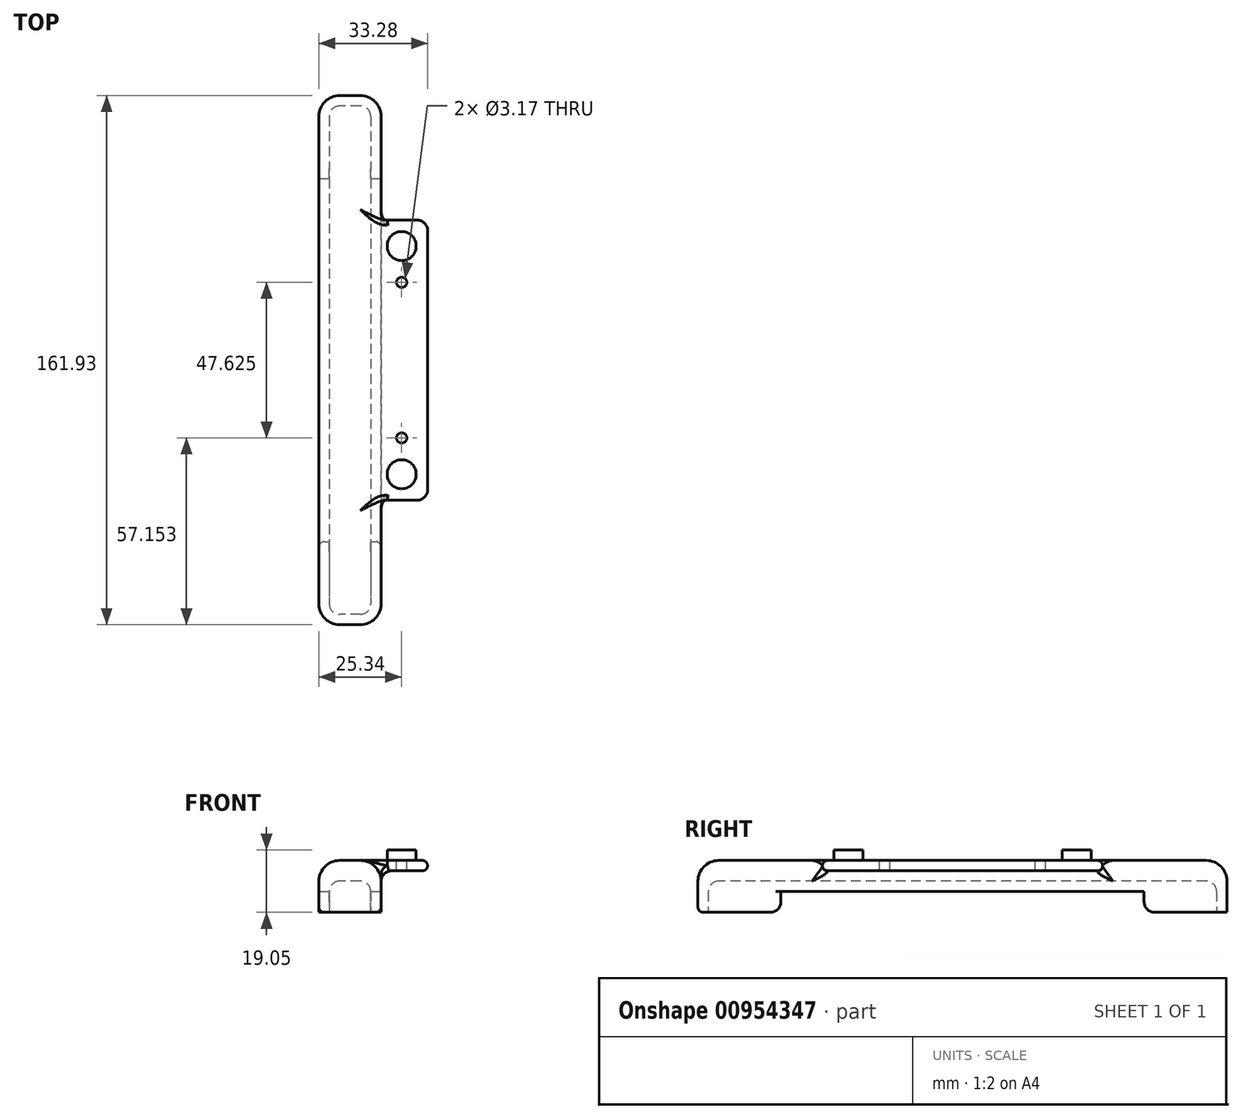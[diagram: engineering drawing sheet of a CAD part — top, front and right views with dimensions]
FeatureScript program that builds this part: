
annotation { "Feature Type Name" : "Feature", "Feature Type Description" : "" }
export const myFeature = defineFeature(function(context is Context, id is Id, definition is map)
    precondition{}
    {
        {
            var Q0;
            Q0=qCreatedBy(makeId("Top.planeOp"),FACE);
            var sketch = newSketch(context, id + "F0", { "sketchPlane" : qUnion([Q0])});
            skLineSegment(sketch, "E0.bottom", {"start": v(7.94, 7.94) * mm, "end": v(-25.34, 7.94) * mm});
            skLineSegment(sketch, "E0.top", {"start": v(7.94, -77.79) * mm, "end": v(-25.34, -77.79) * mm});
            skLineSegment(sketch, "E0.left", {"start": v(7.94, 7.94) * mm, "end": v(7.94, -77.79) * mm});
            skLineSegment(sketch, "E0.right", {"start": v(-25.34, 7.94) * mm, "end": v(-25.34, -77.79) * mm});
            skCircle(sketch, "E1", {"center": v(0, 0) * mm, "radius": 4.45 * mm});
            skCircle(sketch, "E2", {"center": v(0, -69.85) * mm, "radius": 4.45 * mm});
            skSolve(sketch);
        }
        {
            var Q0;
            Q0=makeQuery(id+"F0.imprint","IMPRINT",FACE,{"disambiguationData":[TD([[makeQuery(id+"F0.imprint","IMPRINT",EDGE,{"derivedFrom":sQuery(id+"F0.wireOp",EDGE,"E0.bottom")}),1.0]])]});
            extrude(context, id + "F1", {"entities" : qUnion([Q0]), "depth" : 3.17 * mm, "offsetDistance" : 25.4 * mm});
        }
        {
            var Q0;
            Q0=makeQuery(id+"F1.opExtrude","CAP_FACE",FACE,{"disambiguationData":[OSD([sQuery(id+"F0.wireOp",EDGE,"E0.bottom"),sQuery(id+"F0.wireOp",EDGE,"E0.top"),sQuery(id+"F0.wireOp",EDGE,"E0.left"),sQuery(id+"F0.wireOp",EDGE,"E0.right"),sQuery(id+"F0.wireOp",EDGE,"E1"),sQuery(id+"F0.wireOp",EDGE,"E2"),sQuery(id+"F0.wireOp",EDGE,"2b3a6ad9-cd32-4de6-a3de-1586ba308fc8.0"),sQuery(id+"F0.wireOp",EDGE,"b44657c2-62e0-4c01-9275-96e163e3740f.0"),sQuery(id+"F0.wireOp",EDGE,"936a78f3-9829-4f7b-97c9-a64f973ed5e6.0"),sQuery(id+"F0.wireOp",EDGE,"a6370155-7cf4-457e-acdf-fc1a374a136d.trimOffspring")])],"isStart":true});
            var sketch = newSketch(context, id + "F2", { "sketchPlane" : qUnion([Q0])});
            skCircle(sketch, "E3.0", {"center": v(0, 0) * mm, "radius": 4.45 * mm});
            skCircle(sketch, "E3.1", {"center": v(0, 69.85) * mm, "radius": 4.45 * mm});
            skSolve(sketch);
        }
        {
            var Q0;
            Q0 = qSketchRegion(id + "F2", true);
            extrude(context, id + "F3", {"entities" : qUnion([Q0]), "operationType" : NewBodyOperationType.ADD, "oppositeDirection" : true, "depth" : 6.35 * mm, "offsetDistance" : 25.4 * mm});
        }
        {
            var Q0;
            Q0=makeQuery(id+"F3.boolean.opBoolean","MERGE",FACE,{"derivedFrom":[makeQuery(id+"F1.opExtrude","CAP_FACE",FACE,{"disambiguationData":[OSD([sQuery(id+"F0.wireOp",EDGE,"E0.bottom"),sQuery(id+"F0.wireOp",EDGE,"E0.top"),sQuery(id+"F0.wireOp",EDGE,"E0.left"),sQuery(id+"F0.wireOp",EDGE,"E0.right"),sQuery(id+"F0.wireOp",EDGE,"E1"),sQuery(id+"F0.wireOp",EDGE,"E2")])],"isStart":true}),makeQuery(id+"F3.opExtrude","CAP_FACE",FACE,{"disambiguationData":[OSD([sQuery(id+"F2.wireOp",EDGE,"E3.0")])],"isStart":true}),makeQuery(id+"F3.opExtrude","CAP_FACE",FACE,{"disambiguationData":[OSD([sQuery(id+"F2.wireOp",EDGE,"E3.1")])],"isStart":true})]});
            var sketch = newSketch(context, id + "F4", { "sketchPlane" : qUnion([Q0])});
            skLineSegment(sketch, "E4.bottom", {"start": v(-25.34, -46.04) * mm, "end": v(-6.29, -46.04) * mm});
            skLineSegment(sketch, "E4.top", {"start": v(-25.34, 115.89) * mm, "end": v(-6.29, 115.89) * mm});
            skLineSegment(sketch, "E4.left", {"start": v(-25.34, -46.04) * mm, "end": v(-25.34, 115.89) * mm});
            skLineSegment(sketch, "E4.right", {"start": v(-6.29, -46.04) * mm, "end": v(-6.29, 115.89) * mm});
            skSolve(sketch);
        }
        {
            var Q0;
            Q0 = qSketchRegion(id + "F4", true);
            var Q1;
            Q1=makeQuery(id+"F1.opExtrude","CAP_FACE",FACE,{"disambiguationData":[OSD([sQuery(id+"F0.wireOp",EDGE,"E0.bottom"),sQuery(id+"F0.wireOp",EDGE,"E0.top"),sQuery(id+"F0.wireOp",EDGE,"E0.left"),sQuery(id+"F0.wireOp",EDGE,"E0.right"),sQuery(id+"F0.wireOp",EDGE,"E1"),sQuery(id+"F0.wireOp",EDGE,"E2")])],"isStart":false});
            extrude(context, id + "F5", {"entities" : qUnion([Q0]), "operationType" : NewBodyOperationType.ADD, "depth" : 6.35 * mm, "offsetDistance" : 25.4 * mm, "hasSecondDirection" : true, "secondDirectionBound" : SecondDirectionBoundingType.UP_TO_SURFACE, "secondDirectionOppositeDirection" : true, "secondDirectionDepth" : 25.4 * mm, "secondDirectionBoundEntityFace" : qUnion([Q1])});
        }
        {
            var Q0;
            Q0=makeQuery(id+"F5.opExtrude","CAP_FACE",FACE,{"disambiguationData":[OSD([sQuery(id+"F4.wireOp",EDGE,"E4.bottom"),sQuery(id+"F4.wireOp",EDGE,"E4.top"),sQuery(id+"F4.wireOp",EDGE,"E4.left"),sQuery(id+"F4.wireOp",EDGE,"E4.right")])],"isStart":false});
            var sketch = newSketch(context, id + "F6", { "sketchPlane" : qUnion([Q0])});
            skLineSegment(sketch, "E5.bottom", {"start": v(-25.34, -46.04) * mm, "end": v(-6.29, -46.04) * mm});
            skLineSegment(sketch, "E5.top", {"start": v(-25.34, -20.64) * mm, "end": v(-6.29, -20.64) * mm});
            skLineSegment(sketch, "E5.left", {"start": v(-25.34, -46.04) * mm, "end": v(-25.34, -20.64) * mm});
            skLineSegment(sketch, "E5.right", {"start": v(-6.29, -46.04) * mm, "end": v(-6.29, -20.64) * mm});
            skLineSegment(sketch, "E6.bottom", {"start": v(-25.34, 115.89) * mm, "end": v(-6.29, 115.89) * mm});
            skLineSegment(sketch, "E6.top", {"start": v(-25.34, 90.49) * mm, "end": v(-6.29, 90.49) * mm});
            skLineSegment(sketch, "E6.left", {"start": v(-25.34, 115.89) * mm, "end": v(-25.34, 90.49) * mm});
            skLineSegment(sketch, "E6.right", {"start": v(-6.29, 115.89) * mm, "end": v(-6.29, 90.49) * mm});
            skSolve(sketch);
        }
        {
            var Q0;
            Q0 = qSketchRegion(id + "F6", true);
            extrude(context, id + "F7", {"entities" : qUnion([Q0]), "operationType" : NewBodyOperationType.ADD, "depth" : 6.35 * mm, "offsetDistance" : 25.4 * mm});
        }
        {
            var Q0;
            Q0=makeQuery(id+"F5.boolean.opBoolean","MERGE",EDGE,{"derivedFrom":[makeQuery(id+"F1.opExtrude","CAP_EDGE",EDGE,{"disambiguationData":[OSD([sQuery(id+"F0.wireOp",EDGE,"E0.right")])],"isStart":false}),makeQuery(id+"F5.opExtrude","CAP_EDGE",EDGE,{"disambiguationData":[OSD([sQuery(id+"F4.wireOp",EDGE,"E4.left")])],"isStart":true})]});
            var Q1;
            {var subQ1=sQuery(id+"F4.wireOp",EDGE,"E4.right");var subQ2=sQuery(id+"F0.wireOp",EDGE,"E0.bottom");Q1=makeQuery(id+"F5.boolean.opBoolean","SPLIT",EDGE,{"disambiguationData":[TD([makeQuery(id+"F1.opExtrude","SWEPT_FACE",FACE,{"disambiguationData":[OSD([subQ2])]})])],"derivedFrom":makeQuery(id+"F5.opExtrude","CAP_EDGE",EDGE,{"disambiguationData":[OSD([subQ1])],"isStart":true})});}
            var Q2;
            Q2=makeQuery(id+"F5.opExtrude","CAP_EDGE",EDGE,{"disambiguationData":[OSD([sQuery(id+"F4.wireOp",EDGE,"E4.bottom")])],"isStart":true});
            var Q3;
            Q3=makeQuery(id+"F7.boolean.opBoolean","MERGE",EDGE,{"derivedFrom":[makeQuery(id+"F5.opExtrude","SWEPT_EDGE",EDGE,{"disambiguationData":[OSD([sQuery(id+"F4.wireOp",EDGE,"E4.bottom"),sQuery(id+"F4.wireOp",EDGE,"E4.right")])]}),makeQuery(id+"F7.opExtrude","SWEPT_EDGE",EDGE,{"disambiguationData":[OSD([sQuery(id+"F6.wireOp",EDGE,"E5.bottom"),sQuery(id+"F6.wireOp",EDGE,"E5.right")])]})]});
            var Q4;
            Q4=makeQuery(id+"F7.boolean.opBoolean","MERGE",EDGE,{"derivedFrom":[makeQuery(id+"F5.opExtrude","SWEPT_EDGE",EDGE,{"disambiguationData":[OSD([sQuery(id+"F4.wireOp",EDGE,"E4.bottom"),sQuery(id+"F4.wireOp",EDGE,"E4.left")])]}),makeQuery(id+"F7.opExtrude","SWEPT_EDGE",EDGE,{"disambiguationData":[OSD([sQuery(id+"F6.wireOp",EDGE,"E5.bottom"),sQuery(id+"F6.wireOp",EDGE,"E5.left")])]})]});
            var Q5;
            Q5=makeQuery(id+"F7.boolean.opBoolean","MERGE",EDGE,{"derivedFrom":[makeQuery(id+"F5.opExtrude","SWEPT_EDGE",EDGE,{"disambiguationData":[OSD([sQuery(id+"F4.wireOp",EDGE,"E4.top"),sQuery(id+"F4.wireOp",EDGE,"E4.left")])]}),makeQuery(id+"F7.opExtrude","SWEPT_EDGE",EDGE,{"disambiguationData":[OSD([sQuery(id+"F6.wireOp",EDGE,"E6.bottom"),sQuery(id+"F6.wireOp",EDGE,"E6.left")])]})]});
            fillet(context, id + "F8", {"entities" : qUnion([Q0, Q1, Q2, Q3, Q4, Q5]), "radius" : 6.35 * mm, "allowEdgeOverflow" : false});
        }
        {
            var Q0;
            Q0=makeQuery(id+"F5.opExtrude","CAP_EDGE",EDGE,{"disambiguationData":[OSD([sQuery(id+"F4.wireOp",EDGE,"E4.top")])],"isStart":true});
            fillet(context, id + "F9", {"entities" : qUnion([Q0]), "radius" : 6.35 * mm, "tangentPropagation" : true, "allowEdgeOverflow" : false});
        }
        {
            var Q0;
            Q0=makeQuery(id+"F7.opExtrude","CAP_FACE",FACE,{"disambiguationData":[OSD([sQuery(id+"F6.wireOp",EDGE,"E5.bottom"),sQuery(id+"F6.wireOp",EDGE,"E5.top"),sQuery(id+"F6.wireOp",EDGE,"E5.left"),sQuery(id+"F6.wireOp",EDGE,"E5.right")])],"isStart":false});
            var sketch = newSketch(context, id + "F10", { "sketchPlane" : qUnion([Q0])});
            skLineSegment(sketch, "E7.bottom", {"start": v(-12.64, -42.86) * mm, "end": v(-18.99, -42.86) * mm});
            skLineSegment(sketch, "E7.top", {"start": v(-12.64, 112.71) * mm, "end": v(-18.99, 112.71) * mm});
            skLineSegment(sketch, "E7.left", {"start": v(-9.46, -39.69) * mm, "end": v(-9.46, 109.54) * mm});
            skLineSegment(sketch, "E7.right", {"start": v(-22.16, -39.69) * mm, "end": v(-22.16, 109.54) * mm});
            skPoint(sketch, "E8.visualSharp", {"position": v(-9.46, -42.86) * mm});
            skArc(sketch, "E8.filletArc", {"start": v(-12.64, -42.86) * mm, "mid": v(-10.4, -41.93) * mm, "end": v(-9.46, -39.69) * mm});
            skPoint(sketch, "E9.visualSharp", {"position": v(-22.16, -42.86) * mm});
            skArc(sketch, "E9.filletArc", {"start": v(-22.16, -39.69) * mm, "mid": v(-21.23, -41.93) * mm, "end": v(-18.99, -42.86) * mm});
            skPoint(sketch, "E10.visualSharp", {"position": v(-9.46, 112.71) * mm});
            skArc(sketch, "E10.filletArc", {"start": v(-9.46, 109.54) * mm, "mid": v(-10.4, 111.78) * mm, "end": v(-12.64, 112.71) * mm});
            skPoint(sketch, "E11.visualSharp", {"position": v(-22.16, 112.71) * mm});
            skArc(sketch, "E11.filletArc", {"start": v(-18.99, 112.71) * mm, "mid": v(-21.23, 111.78) * mm, "end": v(-22.16, 109.54) * mm});
            skSolve(sketch);
        }
        {
            var Q0;
            Q0 = qSketchRegion(id + "F10", true);
            extrude(context, id + "F11", {"entities" : qUnion([Q0]), "operationType" : NewBodyOperationType.REMOVE, "oppositeDirection" : true, "depth" : 9.52 * mm, "offsetDistance" : 25.4 * mm});
        }
        {
            var Q0;
            {var subQ0=sQuery(id+"F0.wireOp",EDGE,"E0.top");var subQ2=sQuery(id+"F4.wireOp",EDGE,"E4.right");var subQ3=sQuery(id+"F0.wireOp",EDGE,"E0.bottom");Q0=makeQuery(id+"F8.opFillet","BLEND_EDGE",EDGE,{"blendedFrom":[makeQuery(id+"F5.boolean.opBoolean","SPLIT",EDGE,{"disambiguationData":[TD([makeQuery(id+"F1.opExtrude","SWEPT_FACE",FACE,{"disambiguationData":[OSD([subQ3])]})])],"derivedFrom":makeQuery(id+"F5.opExtrude","CAP_EDGE",EDGE,{"disambiguationData":[OSD([subQ2])],"isStart":true})}),makeQuery(id+"F1.opExtrude","SWEPT_FACE",FACE,{"disambiguationData":[OSD([subQ0])]})],"blendedInto":[makeQuery(id+"F1.opExtrude","SWEPT_FACE",FACE,{"disambiguationData":[OSD([subQ0])]})]});}
            var Q1;
            Q1=makeQuery(id+"F1.opExtrude","SWEPT_EDGE",EDGE,{"disambiguationData":[OSD([sQuery(id+"F0.wireOp",EDGE,"E0.top"),sQuery(id+"F0.wireOp",EDGE,"E0.left")])]});
            var Q2;
            Q2=makeQuery(id+"F1.opExtrude","SWEPT_EDGE",EDGE,{"disambiguationData":[OSD([sQuery(id+"F0.wireOp",EDGE,"E0.bottom"),sQuery(id+"F0.wireOp",EDGE,"E0.left")])]});
            var Q3;
            {var subQ0=sQuery(id+"F0.wireOp",EDGE,"E0.bottom");var subQ1=makeQuery(id+"F1.opExtrude","SWEPT_FACE",FACE,{"disambiguationData":[OSD([subQ0])]});var subQ3=sQuery(id+"F4.wireOp",EDGE,"E4.right");Q3=makeQuery(id+"F8.opFillet","BLEND_EDGE",EDGE,{"blendedFrom":[makeQuery(id+"F5.boolean.opBoolean","SPLIT",EDGE,{"disambiguationData":[TD([subQ1])],"derivedFrom":makeQuery(id+"F5.opExtrude","CAP_EDGE",EDGE,{"disambiguationData":[OSD([subQ3])],"isStart":true})}),subQ1],"blendedInto":[subQ1]});}
            var Q4;
            {var subQ0=sQuery(id+"F6.wireOp",EDGE,"E5.top");Q4=makeQuery(id+"F11.boolean.opBoolean","SPLIT",EDGE,{"disambiguationData":[TD([makeQuery(id+"F1.opExtrude","SWEPT_FACE",FACE,{"disambiguationData":[OSD([sQuery(id+"F0.wireOp",EDGE,"E0.right")])]})])],"derivedFrom":makeQuery(id+"F7.opExtrude","CAP_EDGE",EDGE,{"disambiguationData":[OSD([subQ0])],"isStart":false})});}
            var Q5;
            {var subQ0=sQuery(id+"F6.wireOp",EDGE,"E5.top");Q5=makeQuery(id+"F11.boolean.opBoolean","SPLIT",EDGE,{"disambiguationData":[TD([makeQuery(id+"F1.opExtrude","SWEPT_FACE",FACE,{"disambiguationData":[OSD([sQuery(id+"F0.wireOp",EDGE,"E0.right")])]})])],"derivedFrom":makeQuery(id+"F7.opExtrude","CAP_EDGE",EDGE,{"disambiguationData":[OSD([subQ0])],"isStart":true})});}
            var Q6;
            {var subQ1=sQuery(id+"F6.wireOp",EDGE,"E5.top");Q6=makeQuery(id+"F11.boolean.opBoolean","SPLIT",EDGE,{"disambiguationData":[TD([makeQuery(id+"F5.opExtrude","SWEPT_FACE",FACE,{"disambiguationData":[OSD([sQuery(id+"F4.wireOp",EDGE,"E4.right")])]})])],"derivedFrom":makeQuery(id+"F7.opExtrude","CAP_EDGE",EDGE,{"disambiguationData":[OSD([subQ1])],"isStart":false})});}
            var Q7;
            {var subQ0=sQuery(id+"F4.wireOp",EDGE,"E4.right");var subQ1=sQuery(id+"F6.wireOp",EDGE,"E5.top");Q7=makeQuery(id+"F11.boolean.opBoolean","SPLIT",EDGE,{"disambiguationData":[TD([makeQuery(id+"F5.opExtrude","SWEPT_FACE",FACE,{"disambiguationData":[OSD([subQ0])]})])],"derivedFrom":makeQuery(id+"F7.opExtrude","CAP_EDGE",EDGE,{"disambiguationData":[OSD([subQ1])],"isStart":true})});}
            var Q8;
            {var subQ0=sQuery(id+"F6.wireOp",EDGE,"E6.top");Q8=makeQuery(id+"F11.boolean.opBoolean","SPLIT",EDGE,{"disambiguationData":[TD([makeQuery(id+"F5.opExtrude","SWEPT_FACE",FACE,{"disambiguationData":[OSD([sQuery(id+"F4.wireOp",EDGE,"E4.right")])]})])],"derivedFrom":makeQuery(id+"F7.opExtrude","CAP_EDGE",EDGE,{"disambiguationData":[OSD([subQ0])],"isStart":false})});}
            var Q9;
            {var subQ0=sQuery(id+"F6.wireOp",EDGE,"E6.top");var subQ1=sQuery(id+"F4.wireOp",EDGE,"E4.right");Q9=makeQuery(id+"F11.boolean.opBoolean","SPLIT",EDGE,{"disambiguationData":[TD([makeQuery(id+"F5.opExtrude","SWEPT_FACE",FACE,{"disambiguationData":[OSD([subQ1])]})])],"derivedFrom":makeQuery(id+"F7.opExtrude","CAP_EDGE",EDGE,{"disambiguationData":[OSD([subQ0])],"isStart":true})});}
            var Q10;
            Q10=makeQuery(id+"F11.boolean.opBoolean","COPY",EDGE,{"derivedFrom":makeQuery(id+"F11.opExtrude","CAP_EDGE",EDGE,{"disambiguationData":[OSD([sQuery(id+"F10.wireOp",EDGE,"E7.left")])],"isStart":false})});
            var Q11;
            {var subQ1=sQuery(id+"F6.wireOp",EDGE,"E6.top");Q11=makeQuery(id+"F11.boolean.opBoolean","SPLIT",EDGE,{"disambiguationData":[TD([makeQuery(id+"F1.opExtrude","SWEPT_FACE",FACE,{"disambiguationData":[OSD([sQuery(id+"F0.wireOp",EDGE,"E0.right")])]})])],"derivedFrom":makeQuery(id+"F7.opExtrude","CAP_EDGE",EDGE,{"disambiguationData":[OSD([subQ1])],"isStart":false})});}
            var Q12;
            {var subQ1=sQuery(id+"F6.wireOp",EDGE,"E6.top");Q12=makeQuery(id+"F11.boolean.opBoolean","SPLIT",EDGE,{"disambiguationData":[TD([makeQuery(id+"F1.opExtrude","SWEPT_FACE",FACE,{"disambiguationData":[OSD([sQuery(id+"F0.wireOp",EDGE,"E0.right")])]})])],"derivedFrom":makeQuery(id+"F7.opExtrude","CAP_EDGE",EDGE,{"disambiguationData":[OSD([subQ1])],"isStart":true})});}
            var Q13;
            {var subQ0=sQuery(id+"F0.wireOp",EDGE,"E2");var subQ1=sQuery(id+"F0.wireOp",EDGE,"E1");var subQ2=sQuery(id+"F0.wireOp",EDGE,"E0.right");var subQ3=sQuery(id+"F0.wireOp",EDGE,"E0.left");var subQ4=sQuery(id+"F0.wireOp",EDGE,"E0.top");var subQ5=sQuery(id+"F0.wireOp",EDGE,"E0.bottom");var subQ7=sQuery(id+"F4.wireOp",EDGE,"E4.right");Q13=makeQuery(id+"F8.opFillet","BLEND_EDGE",EDGE,{"blendedFrom":[makeQuery(id+"F5.boolean.opBoolean","SPLIT",EDGE,{"disambiguationData":[TD([makeQuery(id+"F1.opExtrude","SWEPT_FACE",FACE,{"disambiguationData":[OSD([subQ5])]})])],"derivedFrom":makeQuery(id+"F5.opExtrude","CAP_EDGE",EDGE,{"disambiguationData":[OSD([subQ7])],"isStart":true})}),makeQuery(id+"F3.boolean.opBoolean","MERGE",FACE,{"derivedFrom":[makeQuery(id+"F1.opExtrude","CAP_FACE",FACE,{"disambiguationData":[OSD([subQ5,subQ4,subQ3,subQ2,subQ1,subQ0])],"isStart":true}),makeQuery(id+"F3.opExtrude","CAP_FACE",FACE,{"disambiguationData":[OSD([sQuery(id+"F2.wireOp",EDGE,"E3.0")])],"isStart":true}),makeQuery(id+"F3.opExtrude","CAP_FACE",FACE,{"disambiguationData":[OSD([sQuery(id+"F2.wireOp",EDGE,"E3.1")])],"isStart":true})]})],"blendedInto":[makeQuery(id+"F3.boolean.opBoolean","MERGE",FACE,{"derivedFrom":[makeQuery(id+"F1.opExtrude","CAP_FACE",FACE,{"disambiguationData":[OSD([subQ5,subQ4,subQ3,subQ2,subQ1,subQ0])],"isStart":true}),makeQuery(id+"F3.opExtrude","CAP_FACE",FACE,{"disambiguationData":[OSD([sQuery(id+"F2.wireOp",EDGE,"E3.0")])],"isStart":true}),makeQuery(id+"F3.opExtrude","CAP_FACE",FACE,{"disambiguationData":[OSD([sQuery(id+"F2.wireOp",EDGE,"E3.1")])],"isStart":true})]})]});}
            fillet(context, id + "F12", {"entities" : qUnion([Q0, Q1, Q2, Q3, Q4, Q5, Q6, Q7, Q8, Q9, Q10, Q11, Q12, Q13]), "radius" : 3.17 * mm, "tangentPropagation" : true, "allowEdgeOverflow" : false});
        }
        {
            var Q0;
            Q0=makeQuery(id+"F1.opExtrude","CAP_EDGE",EDGE,{"disambiguationData":[OSD([sQuery(id+"F0.wireOp",EDGE,"E0.left")])],"isStart":true});
            var Q1;
            Q1=makeQuery(id+"F1.opExtrude","CAP_EDGE",EDGE,{"disambiguationData":[OSD([sQuery(id+"F0.wireOp",EDGE,"E0.left")])],"isStart":false});
            var Q2;
            Q2=makeQuery(id+"F7.opExtrude","CAP_EDGE",EDGE,{"disambiguationData":[OSD([sQuery(id+"F6.wireOp",EDGE,"E6.right")])],"isStart":false});
            var Q3;
            {var subQ0=sQuery(id+"F10.wireOp",EDGE,"E7.left");Q3=makeQuery(id+"F11.boolean.opBoolean","COPY",EDGE,{"disambiguationData":[topologyDisambiguationEdgeConnected([makeQuery(id+"F7.opExtrude","CAP_FACE",FACE,{"disambiguationData":[OSD([sQuery(id+"F6.wireOp",EDGE,"E6.bottom"),sQuery(id+"F6.wireOp",EDGE,"E6.top"),sQuery(id+"F6.wireOp",EDGE,"E6.left"),sQuery(id+"F6.wireOp",EDGE,"E6.right")])],"isStart":false})])],"derivedFrom":makeQuery(id+"F11.opExtrude","CAP_EDGE",EDGE,{"disambiguationData":[OSD([subQ0])],"isStart":true})});}
            fillet(context, id + "F13", {"entities" : qUnion([Q0, Q1, Q2, Q3]), "radius" : 1.59 * mm, "tangentPropagation" : true, "allowEdgeOverflow" : false});
        }
        {
            var Q0;
            Q0=makeQuery(id+"F5.boolean.opBoolean","MERGE",FACE,{"derivedFrom":[makeQuery(id+"F1.opExtrude","CAP_FACE",FACE,{"disambiguationData":[OSD([sQuery(id+"F0.wireOp",EDGE,"E0.bottom"),sQuery(id+"F0.wireOp",EDGE,"E0.top"),sQuery(id+"F0.wireOp",EDGE,"E0.left"),sQuery(id+"F0.wireOp",EDGE,"E0.right"),sQuery(id+"F0.wireOp",EDGE,"E1"),sQuery(id+"F0.wireOp",EDGE,"E2")])],"isStart":false}),makeQuery(id+"F5.opExtrude","CAP_FACE",FACE,{"disambiguationData":[OSD([sQuery(id+"F4.wireOp",EDGE,"E4.bottom"),sQuery(id+"F4.wireOp",EDGE,"E4.top"),sQuery(id+"F4.wireOp",EDGE,"E4.left"),sQuery(id+"F4.wireOp",EDGE,"E4.right")])],"isStart":true})]});
            var sketch = newSketch(context, id + "F14", { "sketchPlane" : qUnion([Q0])});
            skCircle(sketch, "E12", {"center": v(0, -11.11) * mm, "radius": 1.59 * mm});
            skCircle(sketch, "E13", {"center": v(0, -58.74) * mm, "radius": 1.59 * mm});
            skSolve(sketch);
        }
        {
            var Q0;
            Q0 = qSketchRegion(id + "F14", true);
            extrude(context, id + "F15", {"entities" : qUnion([Q0]), "operationType" : NewBodyOperationType.REMOVE, "endBound" : BoundingType.THROUGH_ALL, "oppositeDirection" : true, "depth" : 25.4 * mm, "offsetDistance" : 25.4 * mm});
        }
    });
